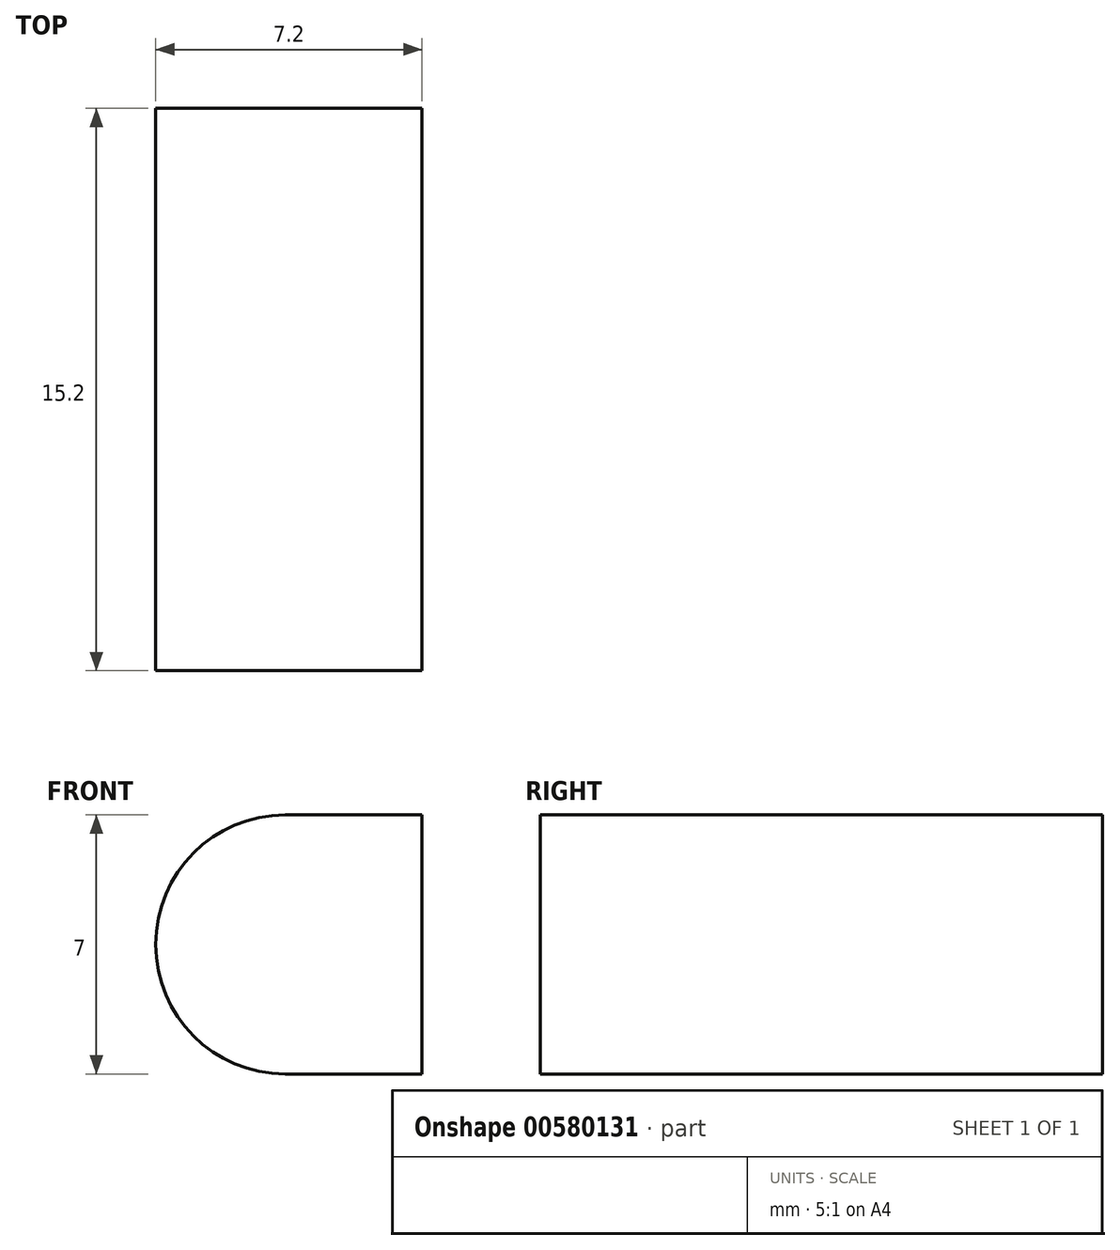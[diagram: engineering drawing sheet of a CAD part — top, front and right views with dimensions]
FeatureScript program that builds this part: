
annotation { "Feature Type Name" : "Feature", "Feature Type Description" : "" }
export const myFeature = defineFeature(function(context is Context, id is Id, definition is map)
    precondition{}
    {
        {
            var Q0;
            Q0=qCreatedBy(makeId("Top.planeOp"),FACE);
            var sketch = newSketch(context, id + "F0", { "sketchPlane" : qUnion([Q0])});
            skLineSegment(sketch, "E0.bottom", {"start": v(-28.4, 25) * mm, "end": v(28.4, 25) * mm});
            skLineSegment(sketch, "E0.top", {"start": v(-28.4, -25) * mm, "end": v(28.4, -25) * mm});
            skLineSegment(sketch, "E0.left", {"start": v(-28.4, 25) * mm, "end": v(-28.4, -25) * mm});
            skLineSegment(sketch, "E0.right", {"start": v(28.4, 25) * mm, "end": v(28.4, -25) * mm});
            skLineSegment(sketch, "E1.bottom", {"start": v(-28.4, -25) * mm, "end": v(-21.2, -25) * mm});
            skLineSegment(sketch, "E1.top", {"start": v(-28.4, -9.8) * mm, "end": v(-21.2, -9.8) * mm});
            skLineSegment(sketch, "E1.left", {"start": v(-28.4, -25) * mm, "end": v(-28.4, -9.8) * mm});
            skLineSegment(sketch, "E1.right", {"start": v(-21.2, -25) * mm, "end": v(-21.2, -9.8) * mm});
            skLineSegment(sketch, "E2.0.1.0", {"start": v(-21.2, 9.8) * mm, "end": v(-21.2, 25) * mm});
            skLineSegment(sketch, "E2.0.1.1", {"start": v(-28.4, 9.8) * mm, "end": v(-28.4, 25) * mm});
            skLineSegment(sketch, "E2.0.1.2", {"start": v(-28.4, 25) * mm, "end": v(-21.2, 25) * mm});
            skLineSegment(sketch, "E2.0.1.3", {"start": v(-28.4, 9.8) * mm, "end": v(-21.2, 9.8) * mm});
            skLineSegment(sketch, "E2.direction1", {"start": v(-28.4, -25) * mm, "end": v(-6.6, -25) * mm, "construction": true});
            skLineSegment(sketch, "E2.direction2", {"start": v(-28.4, -25) * mm, "end": v(-28.4, 9.8) * mm, "construction": true});
            skSolve(sketch);
        }
        {
            var Q0;
            Q0=makeQuery(id+"F0.imprint","IMPRINT",FACE,{"disambiguationData":[TD([[makeQuery(id+"F0.imprint","IMPRINT",EDGE,{"derivedFrom":sQuery(id+"F0.wireOp",EDGE,"E0.bottom")}),-1.0]])]});
            extrude(context, id + "F1", {"entities" : qUnion([Q0]), "depth" : 7 * mm, "offsetDistance" : 25 * mm});
        }
        {
            var Q0;
            Q0=makeQuery(id+"F1.opExtrude","CAP_EDGE",EDGE,{"disambiguationData":[OSD([sQuery(id+"F0.wireOp",EDGE,"E0.left")])],"isStart":false});
            var Q1;
            Q1=makeQuery(id+"F1.opExtrude","CAP_EDGE",EDGE,{"disambiguationData":[OSD([sQuery(id+"F0.wireOp",EDGE,"E0.left")])],"isStart":true});
            fillet(context, id + "F2", {"entities" : qUnion([Q0, Q1]), "radius" : 3.5 * mm, "tangentPropagation" : true, "allowEdgeOverflow" : false});
        }
        {
            var Q0;
            Q0=makeQuery(id+"F1.opExtrude","SWEPT_FACE",FACE,{"disambiguationData":[OSD([sQuery(id+"F0.wireOp",EDGE,"E2.0.1.3")])]});
            var sketch = newSketch(context, id + "F3", { "sketchPlane" : qUnion([Q0])});
            skPoint(sketch, "E3", {"position": v(24.9, 3.5) * mm});
            skSolve(sketch);
        }
        {
            var Q0;
            Q0=sQuery(id+"F3.wireOp",VERTEX,"E3");
            var Q1;
            Q1=makeQuery(id+"F1.opExtrude","SWEPT_BODY",BODY,{"disambiguationData":[OSD([sQuery(id+"F0.wireOp",EDGE,"E0.bottom"),sQuery(id+"F0.wireOp",EDGE,"E0.top"),sQuery(id+"F0.wireOp",EDGE,"E0.left"),sQuery(id+"F0.wireOp",EDGE,"E0.right"),sQuery(id+"F0.wireOp",EDGE,"E1.top"),sQuery(id+"F0.wireOp",EDGE,"E1.right"),sQuery(id+"F0.wireOp",EDGE,"E2.0.1.0"),sQuery(id+"F0.wireOp",EDGE,"E2.0.1.3")])]});
            hole(context, id + "F4", {"style" : HoleStyle.SIMPLE, "endStyle" : HoleEndStyle.THROUGH, "holeDiameter" : 3 * mm, "isTappedThrough" : true, "tappedDepth" : 12 * mm, "tapClearance" : 3, "locations" : qUnion([Q0]), "scope" : qUnion([Q1])});
        }
        {
            var Q0;
            Q0=makeQuery(id+"F1.opExtrude","CAP_FACE",FACE,{"disambiguationData":[OSD([sQuery(id+"F0.wireOp",EDGE,"E0.bottom"),sQuery(id+"F0.wireOp",EDGE,"E0.top"),sQuery(id+"F0.wireOp",EDGE,"E0.left"),sQuery(id+"F0.wireOp",EDGE,"E0.right"),sQuery(id+"F0.wireOp",EDGE,"E1.top"),sQuery(id+"F0.wireOp",EDGE,"E1.right"),sQuery(id+"F0.wireOp",EDGE,"E2.0.1.0"),sQuery(id+"F0.wireOp",EDGE,"E2.0.1.3")])],"isStart":false});
            var sketch = newSketch(context, id + "F5", { "sketchPlane" : qUnion([Q0])});
            skLineSegment(sketch, "E4.bottom", {"start": v(-18.6, 22) * mm, "end": v(25.4, 22) * mm});
            skLineSegment(sketch, "E4.top", {"start": v(-18.6, -22) * mm, "end": v(25.4, -22) * mm});
            skLineSegment(sketch, "E4.left", {"start": v(-18.6, 22) * mm, "end": v(-18.6, -22) * mm});
            skLineSegment(sketch, "E4.right", {"start": v(25.4, 22) * mm, "end": v(25.4, -22) * mm});
            skSolve(sketch);
        }
        {
            var Q0;
            Q0=makeQuery(id+"F5.imprint","IMPRINT",FACE,{"disambiguationData":[TD([[makeQuery(id+"F5.imprint","IMPRINT",EDGE,{"derivedFrom":sQuery(id+"F5.wireOp",EDGE,"E4.bottom")}),-1.0]])]});
            extrude(context, id + "F6", {"entities" : qUnion([Q0]), "operationType" : NewBodyOperationType.REMOVE, "oppositeDirection" : true, "depth" : 5 * mm, "offsetDistance" : 25 * mm});
        }
    });
